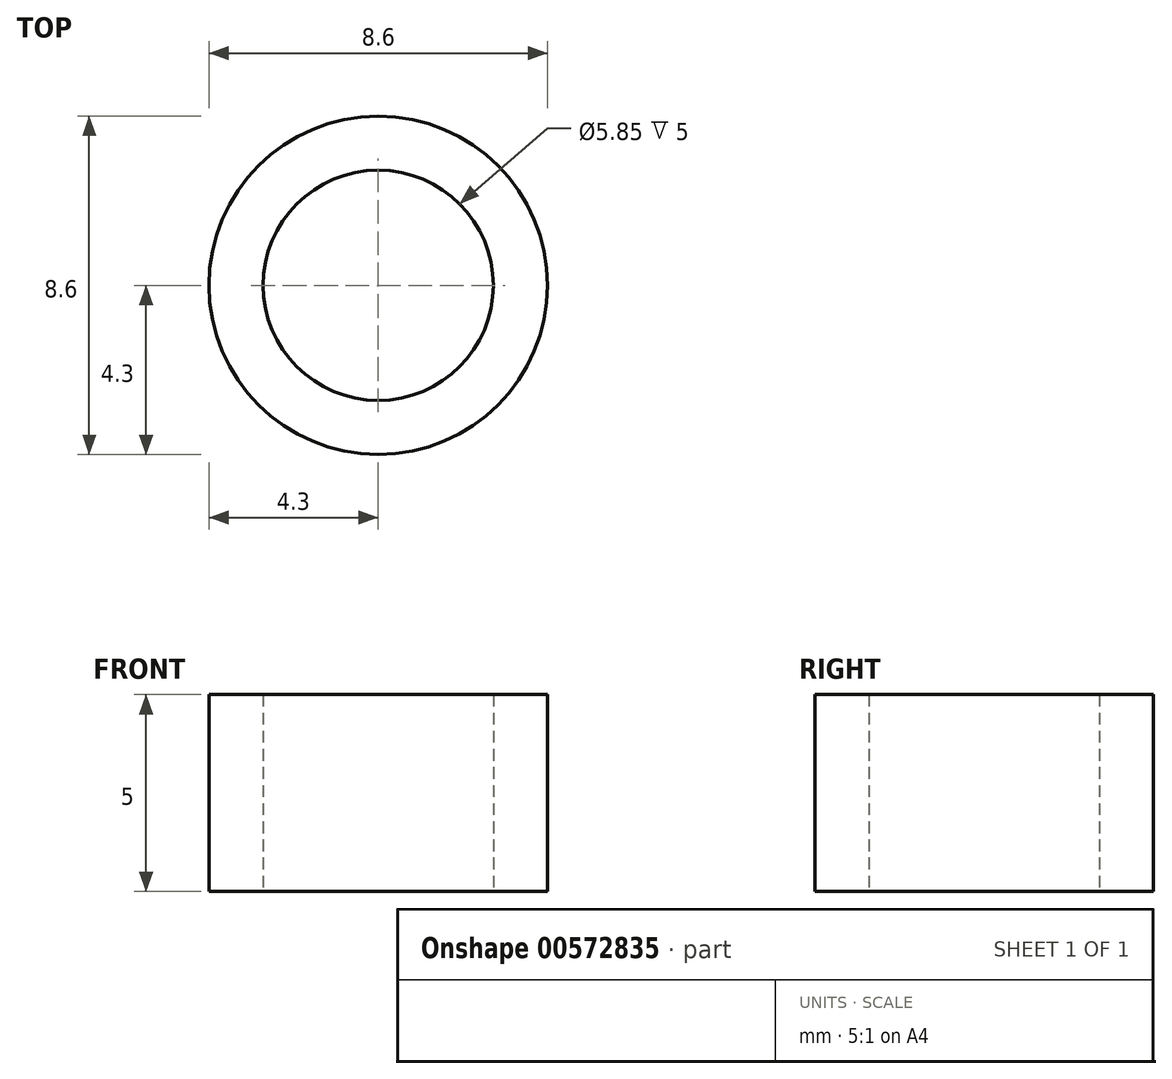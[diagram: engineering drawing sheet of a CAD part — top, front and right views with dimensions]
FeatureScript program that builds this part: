
annotation { "Feature Type Name" : "Feature", "Feature Type Description" : "" }
export const myFeature = defineFeature(function(context is Context, id is Id, definition is map)
    precondition{}
    {
        {
            var Q0;
            Q0=qCreatedBy(makeId("Top.planeOp"),FACE);
            var sketch = newSketch(context, id + "F0", { "sketchPlane" : qUnion([Q0])});
            skCircle(sketch, "E0", {"center": v(0, 0) * mm, "radius": 2.8 * mm});
            skCircle(sketch, "E1", {"center": v(0, 0) * mm, "radius": 4.5 * mm});
            skSolve(sketch);
        }
        {
            var Q0;
            Q0=makeQuery(id+"F0.imprint","IMPRINT",FACE,{"disambiguationData":[TD([[makeQuery(id+"F0.imprint","IMPRINT",EDGE,{"derivedFrom":sQuery(id+"F0.wireOp",EDGE,"E0")}),-1.0]])]});
            extrude(context, id + "F1", {"entities" : qUnion([Q0]), "depth" : 5 * mm, "offsetDistance" : 25 * mm});
        }
        {
            var Q0;
            Q0=makeQuery(id+"F1.opExtrude","CAP_FACE",FACE,{"disambiguationData":[OSD([sQuery(id+"F0.wireOp",EDGE,"E0"),sQuery(id+"F0.wireOp",EDGE,"E1")])],"isStart":false});
            extrude(context, id + "F2", {"entities" : qUnion([Q0]), "operationType" : NewBodyOperationType.REMOVE, "oppositeDirection" : true, "depth" : 5 * mm, "offsetDistance" : 25 * mm});
        }
        {
            var Q0;
            Q0=qCreatedBy(makeId("Top.planeOp"),FACE);
            var sketch = newSketch(context, id + "F3", { "sketchPlane" : qUnion([Q0])});
            skCircle(sketch, "E2", {"center": v(0, 0) * mm, "radius": 2.93 * mm});
            skCircle(sketch, "E3", {"center": v(0, 0) * mm, "radius": 4.3 * mm});
            skSolve(sketch);
        }
        {
            var Q0;
            Q0=makeQuery(id+"F3.imprint","IMPRINT",FACE,{"disambiguationData":[TD([[makeQuery(id+"F3.imprint","IMPRINT",EDGE,{"derivedFrom":sQuery(id+"F3.wireOp",EDGE,"E2")}),-1.0]])]});
            extrude(context, id + "F4", {"entities" : qUnion([Q0]), "depth" : 5 * mm, "offsetDistance" : 25 * mm});
        }
    });
